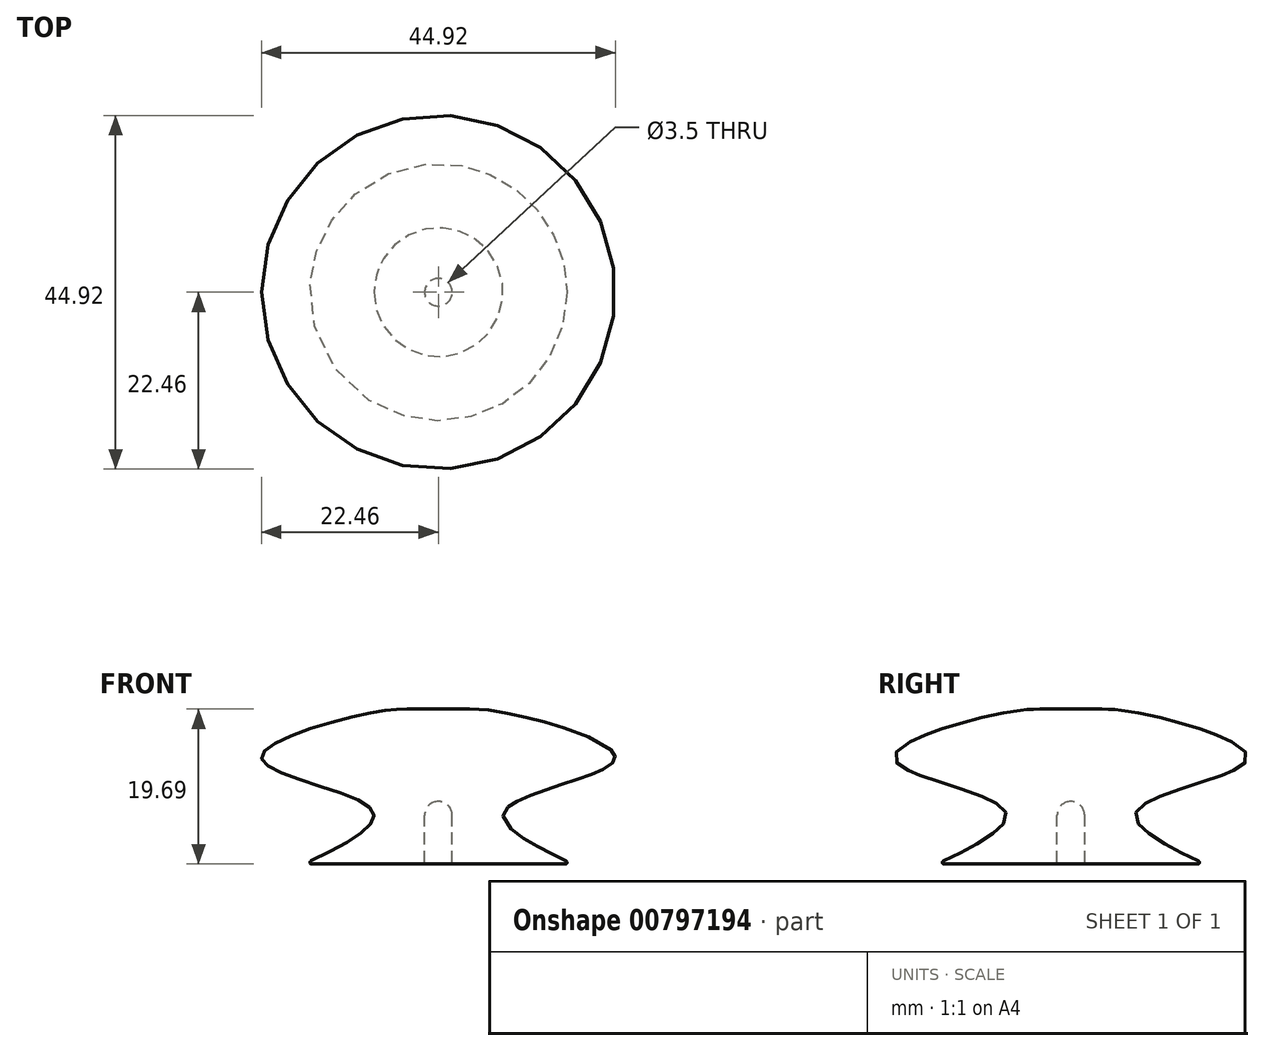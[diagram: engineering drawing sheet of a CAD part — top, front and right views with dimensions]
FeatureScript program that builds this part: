
annotation { "Feature Type Name" : "Feature", "Feature Type Description" : "" }
export const myFeature = defineFeature(function(context is Context, id is Id, definition is map)
    precondition{}
    {
        {
            var Q0;
            Q0=qCreatedBy(makeId("Front.planeOp"),FACE);
            var sketch = newSketch(context, id + "F0", { "sketchPlane" : qUnion([Q0])});
            skLineSegment(sketch, "E0", {"start": v(0, 0) * mm, "end": v(-17, 0) * mm});
            skPoint(sketch, "E1.1.internal.snap0", {"position": v(-8.5, 0) * mm});
            skPoint(sketch, "E1.3.internal.snap0", {"position": v(-8.5, 0) * mm});
            skFitSpline(sketch, "E1", {"points": [v(-17, 0) * mm, v(-8.5, 6.94) * mm, v(-22.43, 13.32) * mm, v(-8.5, 19.22) * mm, v(0, 19.65) * mm], "startDerivative": vector(64.09, 31.21) * mm, "endDerivative": vector(55.8, 0.48) * mm});
            skLineSegment(sketch, "E2", {"start": v(0, 19.65) * mm, "end": v(0, 0) * mm});
            skLineSegment(sketch, "E3.bottom", {"start": v(0, 0) * mm, "end": v(-1.75, 0) * mm});
            skLineSegment(sketch, "E3.left", {"start": v(0, 0) * mm, "end": v(0, 6.2) * mm});
            skLineSegment(sketch, "E3.right", {"start": v(-1.75, 0) * mm, "end": v(-1.75, 6.2) * mm});
            skCircle(sketch, "E4", {"center": v(0, 6.2) * mm, "radius": 1.75 * mm});
            skSolve(sketch);
        }
        {
            var Q0;
            {var subQ1=sQuery(id+"F0.wireOp",EDGE,"E1");Q0=makeQuery(id+"F0.imprint","IMPRINT",FACE,{"disambiguationData":[TD([[makeQuery(id+"F0.imprint","IMPRINT",EDGE,{"derivedFrom":subQ1}),-1.0]])]});}
            var Q1;
            Q1=sQuery(id+"F0.wireOp",EDGE,"E2");
            revolve(context, id + "F1", {"surfaceOperationType" : NewSurfaceOperationType.NEW, "entities" : qUnion([Q0]), "axis" : qUnion([Q1]), "revolveType" : RevolveType.FULL});
        }
        {
            var Q0;
            Q0=makeQuery(id+"F1.opRevolve","SWEPT_EDGE",EDGE,{"disambiguationData":[OSD([sQuery(id+"F0.wireOp",EDGE,"E0"),sQuery(id+"F0.wireOp",EDGE,"E1")])]});
            fillet(context, id + "F2", {"entities" : qUnion([Q0]), "radius" : .2 * mm, "tangentPropagation" : true, "allowEdgeOverflow" : false});
        }
        {
            var Q0;
            Q0=makeQuery(id+"F1.opRevolve","SWEPT_EDGE",EDGE,{"disambiguationData":[OSD([sQuery(id+"F0.wireOp",EDGE,"E0"),sQuery(id+"F0.wireOp",EDGE,"E3.right")])]});
            fillet(context, id + "F3", {"entities" : qUnion([Q0]), "radius" : .2 * mm, "tangentPropagation" : true, "allowEdgeOverflow" : false});
        }
    });
